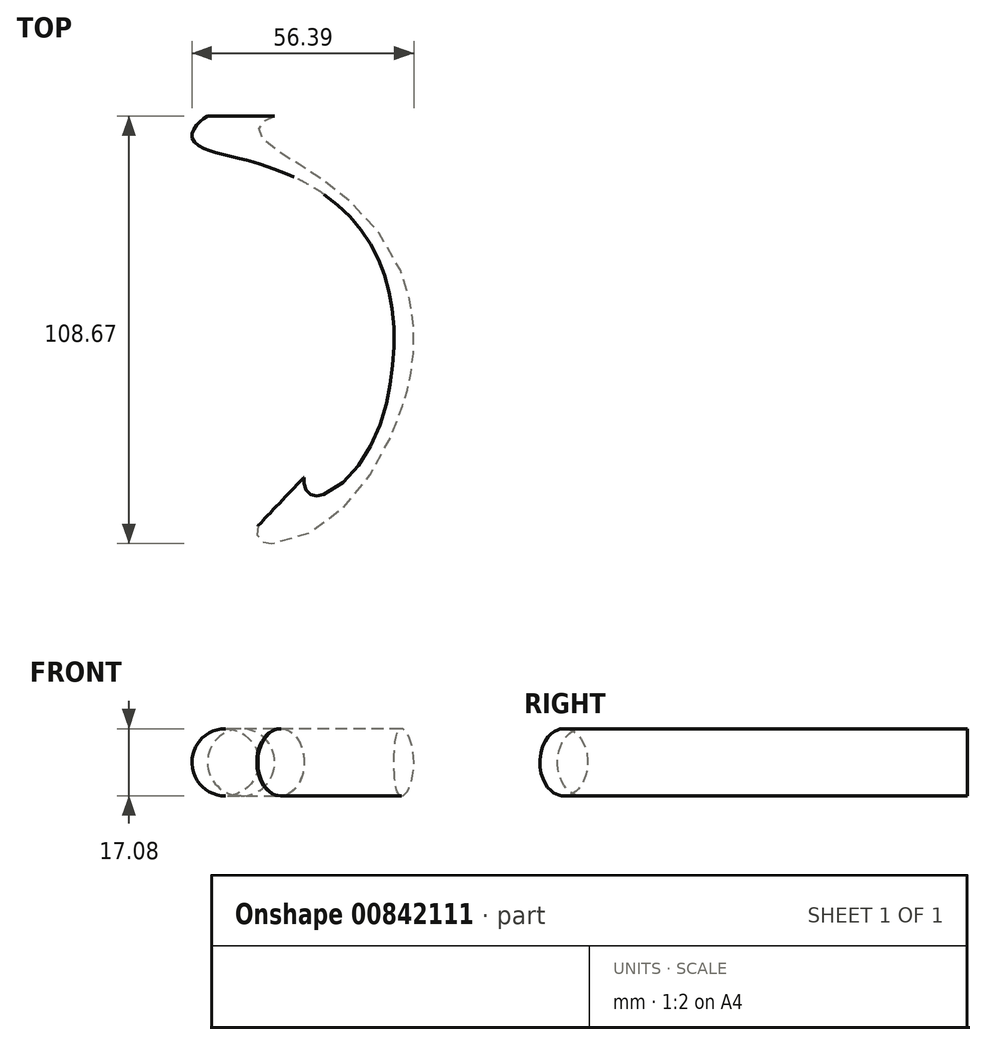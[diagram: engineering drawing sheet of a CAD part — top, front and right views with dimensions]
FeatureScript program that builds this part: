
annotation { "Feature Type Name" : "Feature", "Feature Type Description" : "" }
export const myFeature = defineFeature(function(context is Context, id is Id, definition is map)
    precondition{}
    {
        {
            var Q0;
            Q0=qCreatedBy(makeId("Front.planeOp"),FACE);
            var sketch = newSketch(context, id + "F0", { "sketchPlane" : qUnion([Q0])});
            skCircle(sketch, "E0", {"center": v(0, 0) * mm, "radius": 8.54 * mm});
            skSolve(sketch);
        }
        {
            var Q0;
            Q0=qCreatedBy(makeId("Top.planeOp"),FACE);
            var sketch = newSketch(context, id + "F1", { "sketchPlane" : qUnion([Q0])});
            skLineSegment(sketch, "E1", {"start": v(0, 0) * mm, "end": v(0, -51.05) * mm});
            skFitSpline(sketch, "E2", {"points": [v(0, -51.05) * mm, v(-0.94, -66.18) * mm, v(-15.17, -71.64) * mm, v(-26.85, -62.77) * mm], "startDerivative": vector(0, -44.9) * mm, "endDerivative": vector(-31.45, 29.95) * mm});
            skSolve(sketch);
        }
        {
            var Q0;
            Q0=makeQuery(id+"F0.imprint","IMPRINT",FACE,{"disambiguationData":[TD([[makeQuery(id+"F0.imprint","IMPRINT",EDGE,{"derivedFrom":sQuery(id+"F0.wireOp",EDGE,"E0")}),1.0]])]});
            var Q1;
            Q1=sQuery(id+"F1.wireOp",EDGE,"E2");
            sweep(context, id + "F2", {"profiles" : qUnion([Q0]), "path" : qUnion([Q1])});
        }
    });
